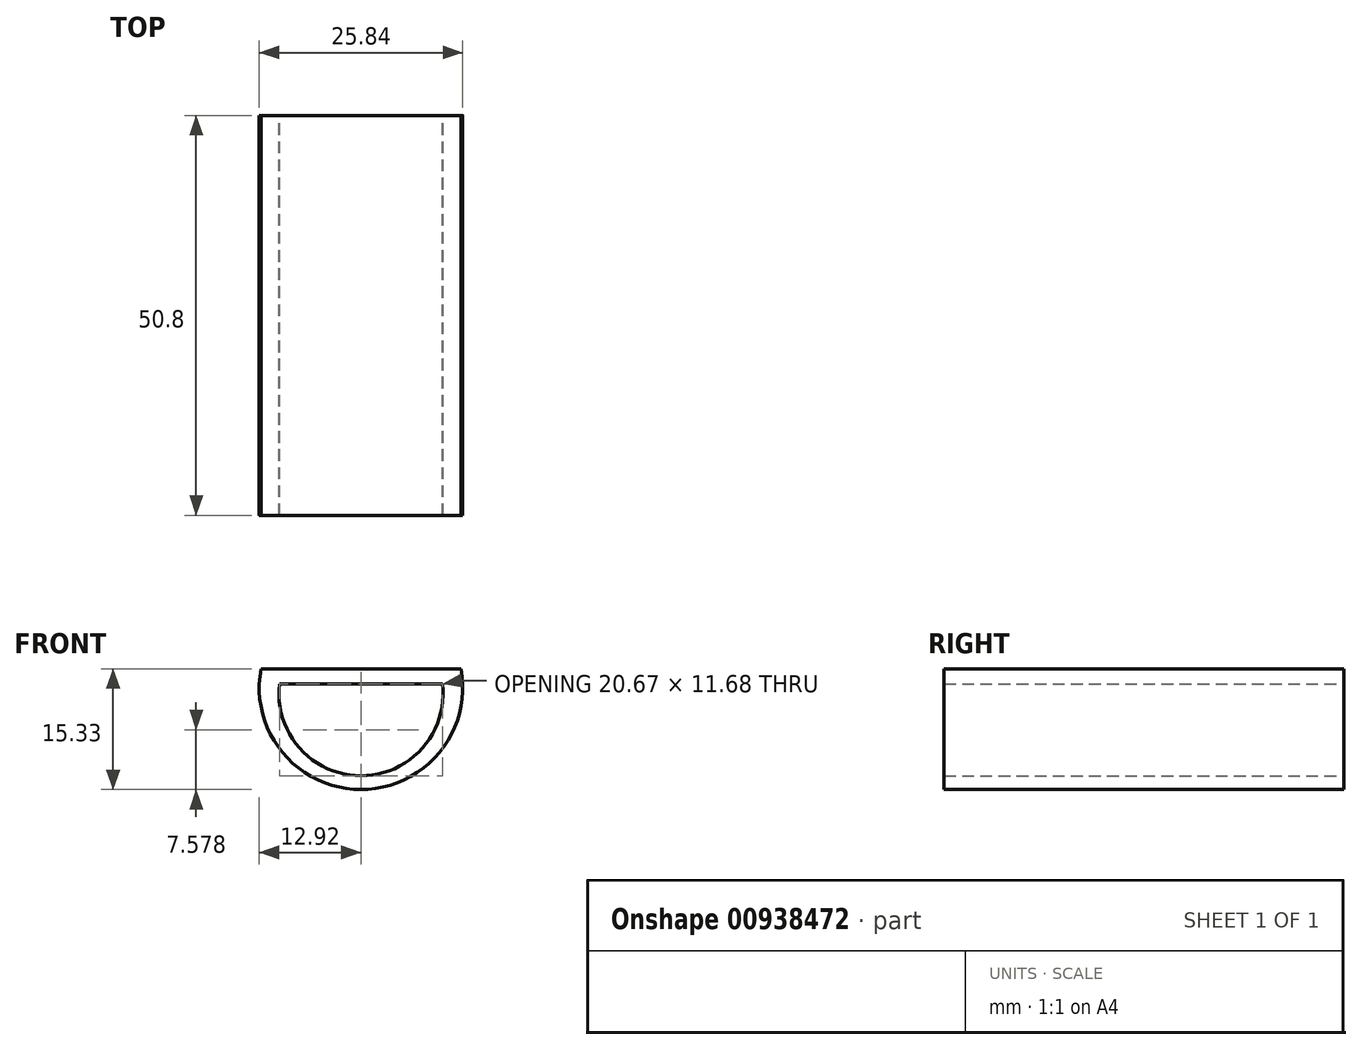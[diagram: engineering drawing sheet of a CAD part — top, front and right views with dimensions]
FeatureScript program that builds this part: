
annotation { "Feature Type Name" : "Feature", "Feature Type Description" : "" }
export const myFeature = defineFeature(function(context is Context, id is Id, definition is map)
    precondition{}
    {
        {
            var Q0;
            Q0=qCreatedBy(makeId("Front.planeOp"),FACE);
            var sketch = newSketch(context, id + "F0", { "sketchPlane" : qUnion([Q0])});
            skLineSegment(sketch, "E0", {"start": v(-10.34, 1.27) * mm, "end": v(10.34, 1.27) * mm});
            skArc(sketch, "E1.MirrorCS", {"start": v(10.34, 1.27) * mm, "mid": v(0, -10.41) * mm, "end": v(-10.34, 1.27) * mm});
            skLineSegment(sketch, "E2", {"start": v(-12.7, 3.17) * mm, "end": v(12.7, 3.17) * mm});
            skArc(sketch, "E3", {"start": v(-12.7, 3.17) * mm, "mid": v(0, -12.15) * mm, "end": v(12.7, 3.17) * mm});
            skSolve(sketch);
        }
        {
            var Q0;
            Q0=makeQuery(id+"F0.imprint","IMPRINT",FACE,{"disambiguationData":[TD([[makeQuery(id+"F0.imprint","IMPRINT",EDGE,{"derivedFrom":sQuery(id+"F0.wireOp",EDGE,"E0")}),1.0]])]});
            extrude(context, id + "F1", {"entities" : qUnion([Q0]), "endBound" : BoundingType.SYMMETRIC, "depth" : 50.8 * mm, "offsetDistance" : 25.4 * mm});
        }
    });
